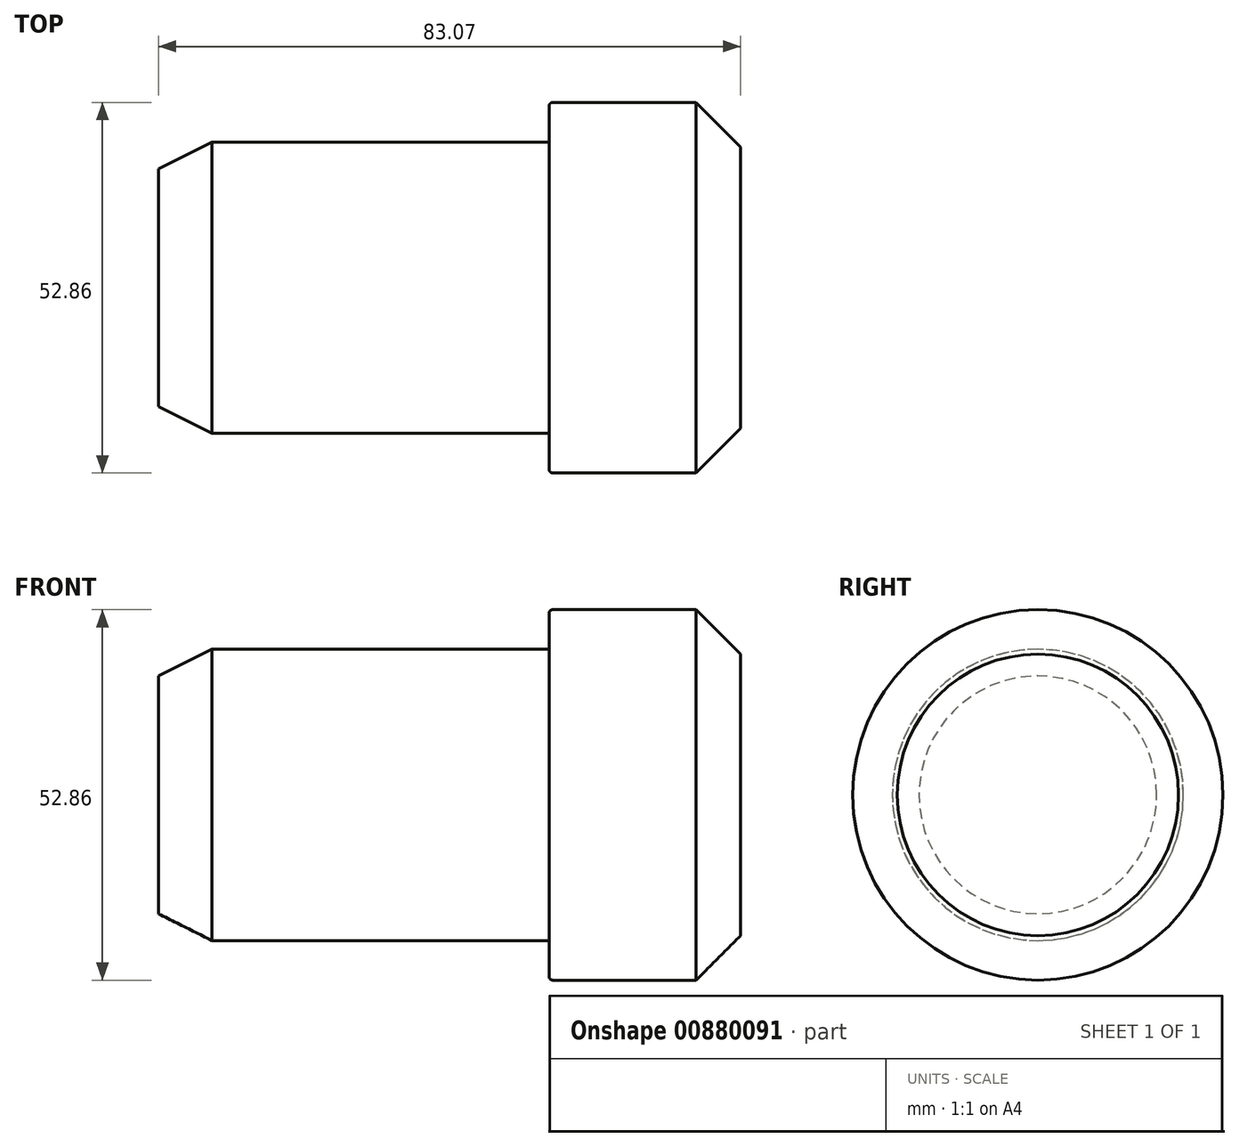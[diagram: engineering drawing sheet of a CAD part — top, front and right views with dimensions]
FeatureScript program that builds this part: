
annotation { "Feature Type Name" : "Feature", "Feature Type Description" : "" }
export const myFeature = defineFeature(function(context is Context, id is Id, definition is map)
    precondition{}
    {
        {
            var Q0;
            Q0=qCreatedBy(makeId("Front.planeOp"),FACE);
            var sketch = newSketch(context, id + "F0", { "sketchPlane" : qUnion([Q0])});
            skLineSegment(sketch, "E0", {"start": v(0, 0) * mm, "end": v(120.98, 0) * mm, "construction": true});
            skLineSegment(sketch, "E1", {"start": v(0, 20.77) * mm, "end": v(55.74, 20.77) * mm});
            skLineSegment(sketch, "E2", {"start": v(55.74, 20.77) * mm, "end": v(55.74, 26.43) * mm});
            skLineSegment(sketch, "E3", {"start": v(55.74, 26.43) * mm, "end": v(83.07, 26.43) * mm});
            skLineSegment(sketch, "E4", {"start": v(83.07, 26.43) * mm, "end": v(83.07, 0) * mm});
            skLineSegment(sketch, "E5", {"start": v(83.07, 0) * mm, "end": v(0, 0) * mm});
            skLineSegment(sketch, "E6", {"start": v(0, 20.77) * mm, "end": v(0, 0) * mm});
            skSolve(sketch);
        }
        {
            var Q0;
            Q0 = qSketchRegion(id + "F0", true);
            var Q1;
            Q1=sQuery(id+"F0.wireOp",EDGE,"E0");
            revolve(context, id + "F1", {"surfaceOperationType" : NewSurfaceOperationType.NEW, "entities" : qUnion([Q0]), "axis" : qUnion([Q1]), "revolveType" : RevolveType.FULL});
        }
        {
            var Q0;
            Q0=makeQuery(id+"F1.opRevolve","SWEPT_EDGE",EDGE,{"disambiguationData":[OSD([sQuery(id+"F0.wireOp",EDGE,"E2"),sQuery(id+"F0.wireOp",EDGE,"E3")])]});
            fillet(context, id + "F2", {"entities" : qUnion([Q0]), "radius" : 0.5 * mm, "tangentPropagation" : true, "allowEdgeOverflow" : false});
        }
        {
            var Q0;
            Q0=makeQuery(id+"F1.opRevolve","SWEPT_EDGE",EDGE,{"disambiguationData":[OSD([sQuery(id+"F0.wireOp",EDGE,"E3"),sQuery(id+"F0.wireOp",EDGE,"E4")])]});
            chamfer(context, id + "F3", {"entities" : qUnion([Q0]), "width" : 6.35 * mm, "tangentPropagation" : true});
        }
        {
            var Q0;
            Q0=makeQuery(id+"F1.opRevolve","SWEPT_EDGE",EDGE,{"disambiguationData":[OSD([sQuery(id+"F0.wireOp",EDGE,"E1"),sQuery(id+"F0.wireOp",EDGE,"E6")])]});
            chamfer(context, id + "F4", {"entities" : qUnion([Q0]), "chamferType" : ChamferType.TWO_OFFSETS, "width1" : 3.8 * mm, "oppositeDirection" : false, "width2" : 7.62 * mm, "tangentPropagation" : true});
        }
    });
